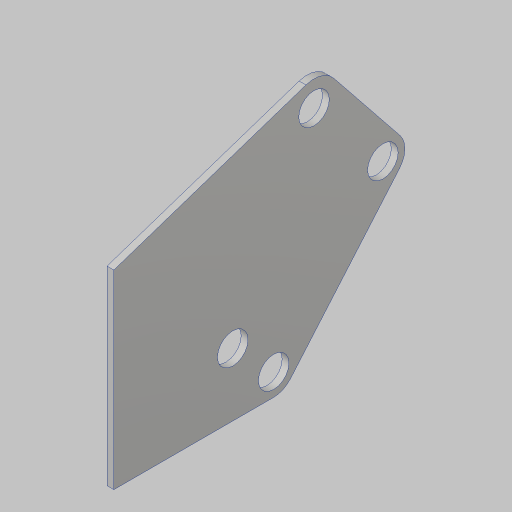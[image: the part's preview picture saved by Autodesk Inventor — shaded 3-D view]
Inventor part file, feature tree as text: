
AUTODESK INVENTOR PART (.ipt)
format: ipt  version: 2023.5 (Build 275446000, 446)  size: 153,600 bytes
history: native  units: in
note: dims shown in document units (in); Inventor stores cm internally (conversion verified against a paired STEP export)
features: sketch x2, extrude x1
ambient origin geometry x8: Origin, YZ Plane, XZ Plane, XY Plane, X Axis, Y Axis, Z Axis, Center Point
bodies: Solid1 (feature_tree)
feature tree (3):
  sketch  "Sketch1"  dims[d0=2.0in d1=16.0in]
  extrude  "Extrusion1"  Depth=16.0in
  sketch  "Sketch2"  dims[d2=0.75in d3=5.75in d4=3.0in d5=1.375in d6=4.5in d7=0.5in d8=1.375in d9=1.0in d10=2.0in d11=1.375in d12=2.126in d13=2.5in d14=4.5in d15=3.0in d16=4.5in d17=0.25in d18=3.0in d19=0.25in d20=0.25in d21=4.5in d22=3.898in d23=5.7in d24=1.125in d27=0.375in d28=0.25in d29=0.25in d31=0.25in d32=0.0in d33=6.9in d34=6.85in d35=7.0in]
